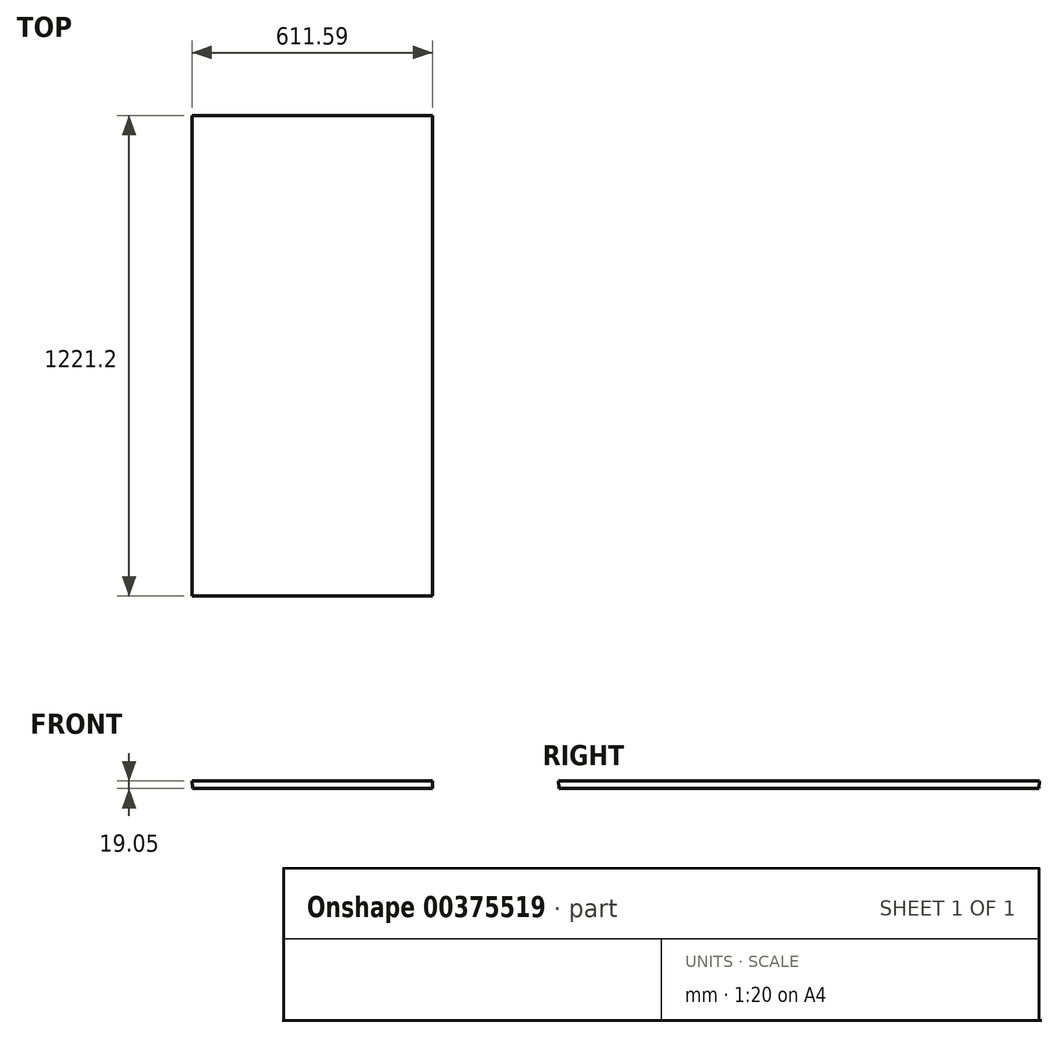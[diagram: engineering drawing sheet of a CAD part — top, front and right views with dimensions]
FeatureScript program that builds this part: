
annotation { "Feature Type Name" : "Feature", "Feature Type Description" : "" }
export const myFeature = defineFeature(function(context is Context, id is Id, definition is map)
    precondition{}
    {
        {
            var Q0;
            Q0=qCreatedBy(makeId("Top.planeOp"),FACE);
            var sketch = newSketch(context, id + "F0", { "sketchPlane" : qUnion([Q0])});
            skLineSegment(sketch, "E0.bottom", {"start": v(352.07, -665.02) * mm, "end": v(-257.53, -665.02) * mm});
            skLineSegment(sketch, "E0.top", {"start": v(352.07, 554.18) * mm, "end": v(-257.53, 554.18) * mm});
            skLineSegment(sketch, "E0.left", {"start": v(352.07, -665.02) * mm, "end": v(352.07, 554.18) * mm});
            skLineSegment(sketch, "E0.right", {"start": v(-257.53, -665.02) * mm, "end": v(-257.53, 554.18) * mm});
            skPoint(sketch, "E0.middle", {"position": v(47.27, -55.42) * mm});
            skSolve(sketch);
        }
        {
            var Q0;
            Q0 = qSketchRegion(id + "F0", true);
            var Q1;
            Q1=qCreatedBy(makeId("Top.planeOp"),FACE);
            var Q2;
            Q2=qCreatedBy(makeId("Origin.pointOp"),VERTEX);
            extrude(context, id + "F1", {"entities" : qUnion([Q0]), "depth" : 19.05 * mm, "hasDraft" : true, "draftAngle" : 3 * degree});
        }
    });
